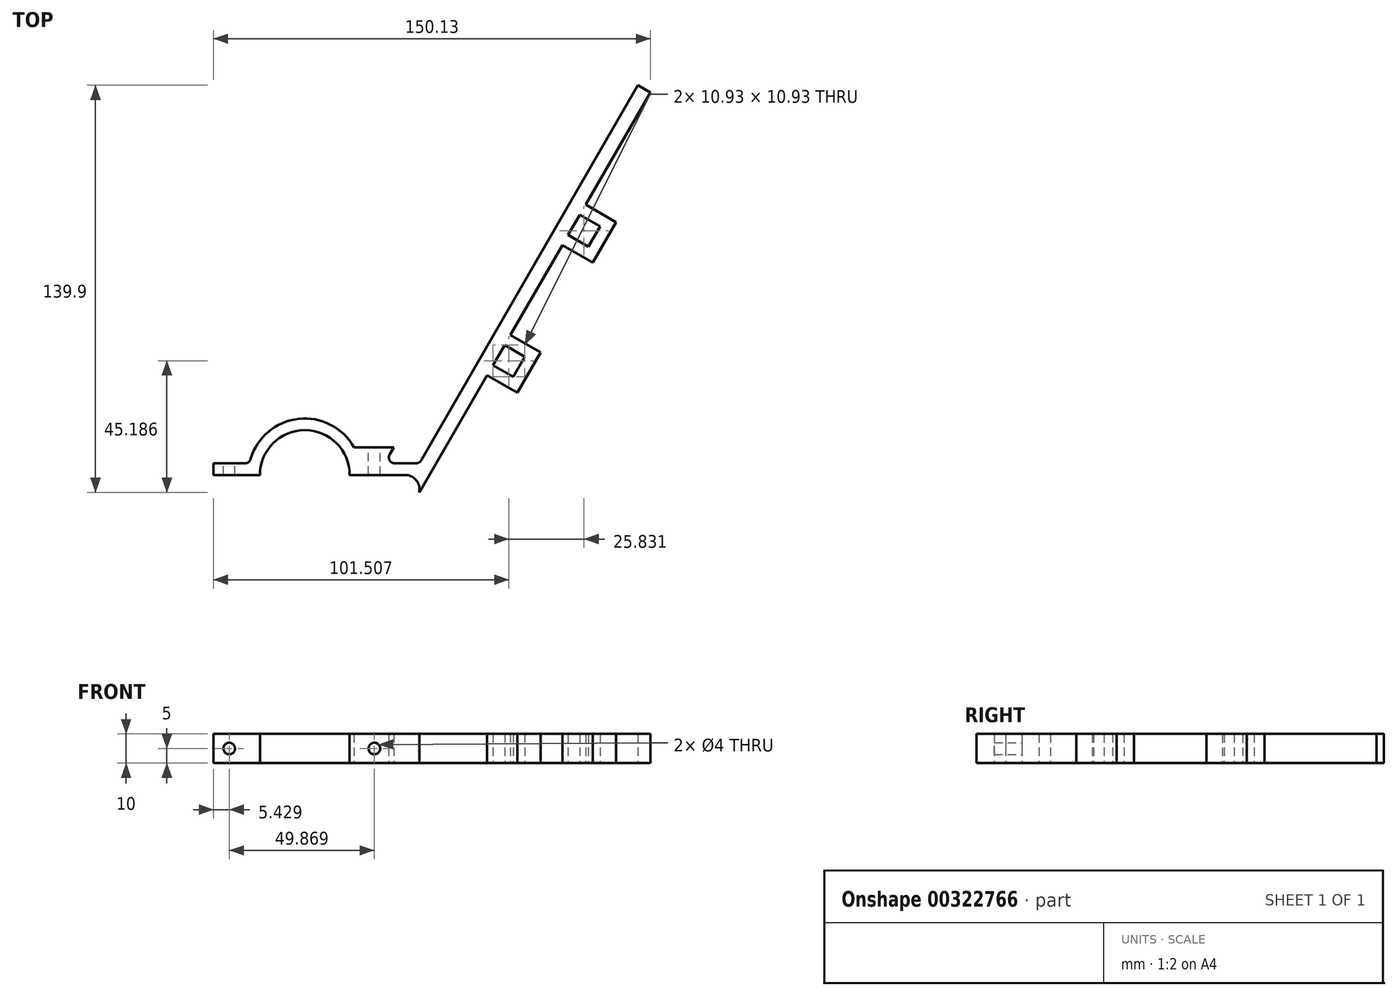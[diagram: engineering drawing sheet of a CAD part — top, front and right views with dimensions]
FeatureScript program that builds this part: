
annotation { "Feature Type Name" : "Feature", "Feature Type Description" : "" }
export const myFeature = defineFeature(function(context is Context, id is Id, definition is map)
    precondition{}
    {
        {
            var Q0;
            Q0=qCreatedBy(makeId("Top.planeOp"),FACE);
            var sketch = newSketch(context, id + "F0", { "sketchPlane" : qUnion([Q0])});
            skArc(sketch, "E0", {"start": v(15.4, 0) * mm, "mid": v(0, 15.4) * mm, "end": v(-15.4, 0) * mm});
            skArc(sketch, "E1.0", {"start": v(18.98, 4) * mm, "mid": v(0.74, 19.39) * mm, "end": v(-18.62, 5.44) * mm});
            skLineSegment(sketch, "E2", {"start": v(-19.4, 0) * mm, "end": v(-15.4, 0) * mm});
            skLineSegment(sketch, "E3.trimOffspring", {"start": v(15.4, 0) * mm, "end": v(19.4, 0) * mm});
            skLineSegment(sketch, "E4", {"start": v(-19.4, 0) * mm, "end": v(-31.4, 0) * mm});
            skLineSegment(sketch, "E5", {"start": v(-31.4, 0) * mm, "end": v(-31.4, 4) * mm});
            skLineSegment(sketch, "E6", {"start": v(-31.4, 4) * mm, "end": v(-20.54, 4) * mm});
            skLineSegment(sketch, "E7", {"start": v(19.4, 0) * mm, "end": v(34.4, 0) * mm});
            skLineSegment(sketch, "E8", {"start": v(39.4, 0) * mm, "end": v(39.4, 4) * mm});
            skLineSegment(sketch, "E9", {"start": v(38.25, 4) * mm, "end": v(30.86, 4) * mm});
            skLineSegment(sketch, "E10", {"start": v(39.98, 5) * mm, "end": v(114.4, 133.9) * mm});
            skLineSegment(sketch, "E11", {"start": v(114.4, 133.9) * mm, "end": v(116.13, 132.9) * mm});
            skLineSegment(sketch, "E12", {"start": v(116.13, 132.9) * mm, "end": v(118.73, 131.4) * mm});
            skLineSegment(sketch, "E13", {"start": v(118.73, 131.4) * mm, "end": v(39.4, -6) * mm});
            skLineSegment(sketch, "E14", {"start": v(39.4, -5) * mm, "end": v(39.4, -6) * mm});
            skPoint(sketch, "E15.visualSharp", {"position": v(39.4, 0) * mm});
            skArc(sketch, "E15.filletArc", {"start": v(39.4, -5) * mm, "mid": v(37.94, -1.46) * mm, "end": v(34.4, 0) * mm});
            skLineSegment(sketch, "E16", {"start": v(29.13, 7) * mm, "end": v(30.6, 9.53) * mm});
            skLineSegment(sketch, "E17", {"start": v(30.6, 9.53) * mm, "end": v(16.9, 9.53) * mm});
            skPoint(sketch, "E18.visualSharp", {"position": v(39.4, 4) * mm});
            skArc(sketch, "E18.filletArc", {"start": v(38.25, 4) * mm, "mid": v(39.25, 4.27) * mm, "end": v(39.98, 5) * mm});
            skArc(sketch, "E19.filletArc", {"start": v(29.13, 7) * mm, "mid": v(29.13, 5) * mm, "end": v(30.86, 4) * mm});
            skPoint(sketch, "E20.visualSharp", {"position": v(-18.98, 4) * mm});
            skArc(sketch, "E20.filletArc", {"start": v(-20.54, 4) * mm, "mid": v(-19.34, 4.4) * mm, "end": v(-18.62, 5.44) * mm});
            skLineSegment(sketch, "E21", {"start": v(96.47, 92.85) * mm, "end": v(106.87, 86.85) * mm});
            skLineSegment(sketch, "E22", {"start": v(106.87, 86.85) * mm, "end": v(98.87, 73) * mm});
            skLineSegment(sketch, "E23", {"start": v(98.87, 73) * mm, "end": v(88.47, 79) * mm});
            skLineSegment(sketch, "E24.0", {"start": v(101.4, 85.4) * mm, "end": v(97.4, 78.46) * mm});
            skLineSegment(sketch, "E25.0", {"start": v(97.4, 78.46) * mm, "end": v(90.47, 82.46) * mm});
            skLineSegment(sketch, "E26.0", {"start": v(94.47, 89.4) * mm, "end": v(101.4, 85.4) * mm});
            skLineSegment(sketch, "E27", {"start": v(70.64, 48.11) * mm, "end": v(81.04, 42.11) * mm});
            skLineSegment(sketch, "E28", {"start": v(81.04, 42.11) * mm, "end": v(73.04, 28.26) * mm});
            skLineSegment(sketch, "E29", {"start": v(73.04, 28.26) * mm, "end": v(62.64, 34.26) * mm});
            skLineSegment(sketch, "E30.0", {"start": v(75.57, 40.65) * mm, "end": v(71.57, 33.72) * mm});
            skLineSegment(sketch, "E31.0", {"start": v(71.57, 33.72) * mm, "end": v(64.64, 37.72) * mm});
            skLineSegment(sketch, "E32.0", {"start": v(68.64, 44.65) * mm, "end": v(75.57, 40.65) * mm});
            skSolve(sketch);
        }
        {
            var Q0;
            Q0 = qSketchRegion(id + "F0", true);
            extrude(context, id + "F1", {"entities" : qUnion([Q0]), "depth" : 10 * mm});
        }
        {
            var Q0;
            Q0=makeQuery(id+"F1.opExtrude","SWEPT_FACE",FACE,{"disambiguationData":[OSD([sQuery(id+"F0.wireOp",EDGE,"E6")])]});
            var sketch = newSketch(context, id + "F2", { "sketchPlane" : qUnion([Q0])});
            skCircle(sketch, "E33", {"center": v(25.97, 5) * mm, "radius": 2 * mm});
            skSolve(sketch);
        }
        {
            var Q0;
            Q0 = qSketchRegion(id + "F2", true);
            extrude(context, id + "F3", {"entities" : qUnion([Q0]), "operationType" : NewBodyOperationType.REMOVE, "endBound" : BoundingType.THROUGH_ALL, "oppositeDirection" : true, "depth" : 25 * mm});
        }
        {
            var Q0;
            Q0=makeQuery(id+"F1.opExtrude","SWEPT_FACE",FACE,{"disambiguationData":[OSD([sQuery(id+"F0.wireOp",EDGE,"E17")])]});
            var sketch = newSketch(context, id + "F4", { "sketchPlane" : qUnion([Q0])});
            skCircle(sketch, "E34", {"center": v(-23.9, 5) * mm, "radius": 2 * mm});
            skSolve(sketch);
        }
        {
            var Q0;
            Q0 = qSketchRegion(id + "F4", true);
            extrude(context, id + "F5", {"entities" : qUnion([Q0]), "operationType" : NewBodyOperationType.REMOVE, "endBound" : BoundingType.THROUGH_ALL, "oppositeDirection" : true, "depth" : 25 * mm});
        }
    });
